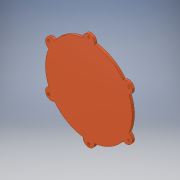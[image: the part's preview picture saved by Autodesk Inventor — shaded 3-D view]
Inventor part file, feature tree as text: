
AUTODESK INVENTOR PART (.ipt)
format: ipt  version: 2017 (Build 210142000, 142)  size: 137,216 bytes
history: native  units: in
note: dims shown in document units (in); Inventor stores cm internally (conversion verified against a paired STEP export)
features: extrude x1, sketch x1
ambient origin geometry x8: Origin, YZ Plane, XZ Plane, XY Plane, X Axis, Y Axis, Z Axis, Center Point
bodies: Solid1 (feature_tree)
feature tree (2):
  extrude  "Extrusion1"  Depth=2.2008in
  sketch  "Sketch2"  dims[d0=0.5906in d7=4.4016in d12=0.1181in d13=2.3622in d15=360.0deg d17=0.1181in d18=0.0in d20=2.2008in d21=0.0394in]
